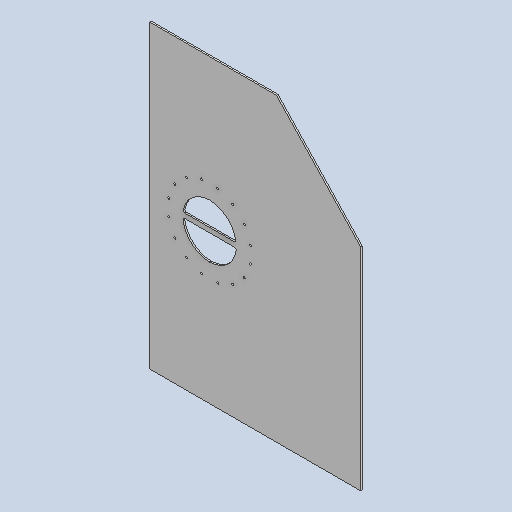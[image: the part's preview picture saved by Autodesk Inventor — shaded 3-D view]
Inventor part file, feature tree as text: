
AUTODESK INVENTOR PART (.ipt)
format: ipt  version: 2025 (Build 290162010, 162A)  size: 270,848 bytes
history: native  units: mm
features: extrude x3, sketch x2, fillet x1, pattern_circular x1, projected_geometry x1, other x1
ambient origin geometry x8: Origin, YZ Plane, XZ Plane, XY Plane, X Axis, Y Axis, Z Axis, Center Point
bodies: Solid1 (feature_tree)
feature tree (9):
  extrude  "Extrusion1"  Depth=1180.0mm
  fillet  "Fillet1"  Radius=1180.0mm
  extrude  "Extrusion4"  Depth=10.0mm
  pattern_circular  "Circular Pattern3"  Count=191  [1 undecoded]
  extrude  "Extrusion5"  [1 undecoded]
  sketch  "Sketch4"  dims[d1=840.0mm d3=1150.0mm d12=1180.0mm]
  sketch  "Sketch5"  dims[d13=950.0mm d14=110.0mm d15=1910.0mm d17=-521.637743mm d18=377.0mm d19=-269.216713mm d24=10.0mm d25=0.0mm d34=380.0mm d35=80.0mm d37=2140.0mm d52=530.0mm d53=5.0mm d54=10.0mm d55=30.0mm d56=10.0mm d59=265.0mm d60=13.0mm d61=1.963495mm d62=10.0mm d63=0.0mm d64=160.0mm d65=360.0deg d67=5.0mm d68=5.0mm d69=780.0mm d71=1078.0mm d72=340.0mm d73=1340.0mm d74=10.0mm d75=0.0mm d70=0.872665mm]
  projected_geometry  "Projected Loop1"
  other  "Definition1"
note: 2 required parameter values undecoded (feature->parameter linkage not recoverable at this tier; creation-order binding heuristic only, values carry confidence <= 0.55)
